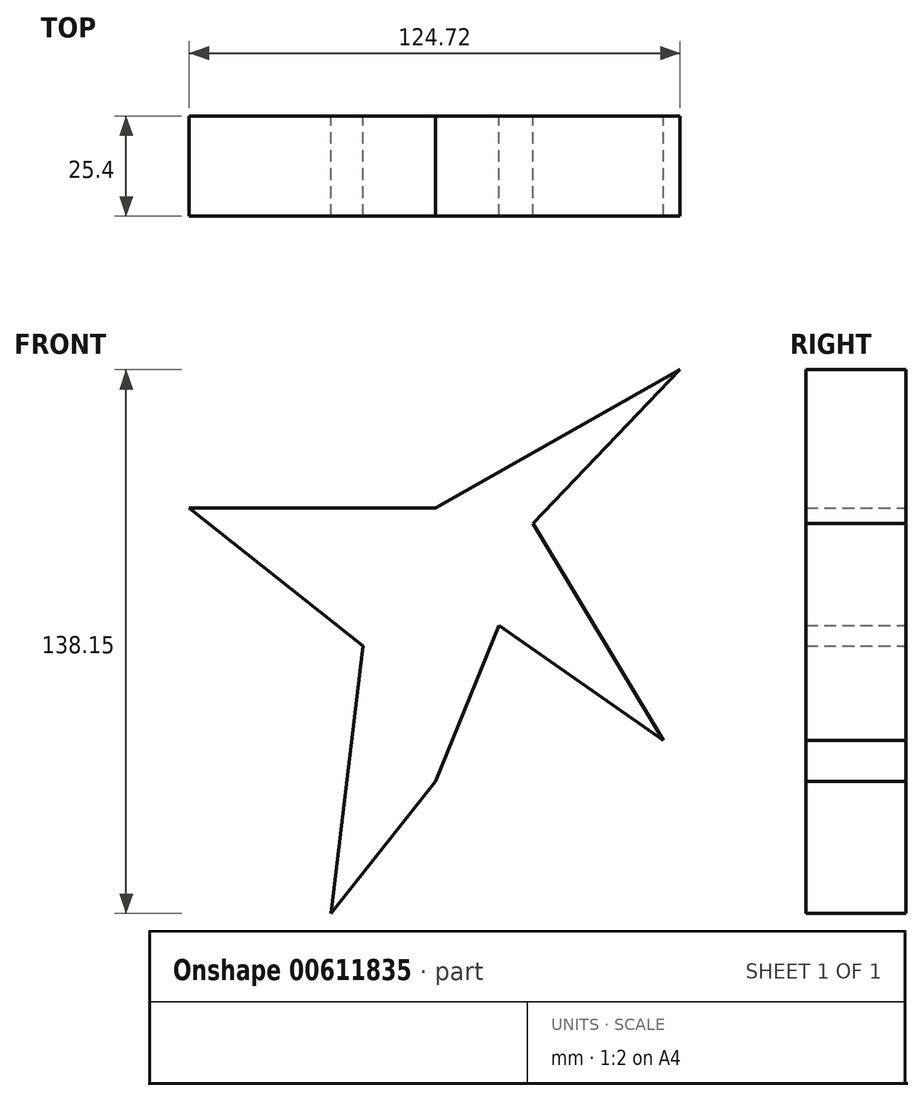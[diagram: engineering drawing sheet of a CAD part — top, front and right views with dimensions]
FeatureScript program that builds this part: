
annotation { "Feature Type Name" : "Feature", "Feature Type Description" : "" }
export const myFeature = defineFeature(function(context is Context, id is Id, definition is map)
    precondition{}
    {
        {
            var Q0;
            Q0=qCreatedBy(makeId("Front.planeOp"),FACE);
            var sketch = newSketch(context, id + "F0", { "sketchPlane" : qUnion([Q0])});
            skLineSegment(sketch, "E0", {"start": v(0, 0) * mm, "end": v(16.16, 39.63) * mm});
            skLineSegment(sketch, "E1", {"start": v(16.16, 39.63) * mm, "end": v(57.84, 10.46) * mm});
            skLineSegment(sketch, "E2", {"start": v(57.84, 10.46) * mm, "end": v(24.78, 65.6) * mm});
            skLineSegment(sketch, "E3", {"start": v(24.78, 65.6) * mm, "end": v(62.15, 104.65) * mm});
            skLineSegment(sketch, "E4", {"start": v(62.15, 104.65) * mm, "end": v(0, 69.54) * mm});
            skLineSegment(sketch, "E5", {"start": v(0, 69.54) * mm, "end": v(-62.57, 69.54) * mm});
            skLineSegment(sketch, "E6", {"start": v(-62.57, 69.54) * mm, "end": v(-18.4, 34.49) * mm});
            skLineSegment(sketch, "E7", {"start": v(-18.4, 34.49) * mm, "end": v(-26.61, -33.5) * mm});
            skLineSegment(sketch, "E8", {"start": v(-26.61, -33.5) * mm, "end": v(0, 0) * mm});
            skSolve(sketch);
        }
        {
            var Q0;
            Q0=makeQuery(id+"F0.imprint","IMPRINT",FACE,{"disambiguationData":[TD([[makeQuery(id+"F0.imprint","IMPRINT",EDGE,{"derivedFrom":sQuery(id+"F0.wireOp",EDGE,"E0")}),1.0]])]});
            extrude(context, id + "F1", {"entities" : qUnion([Q0]), "depth" : 25.4 * mm, "offsetDistance" : 25.4 * mm});
        }
    });
